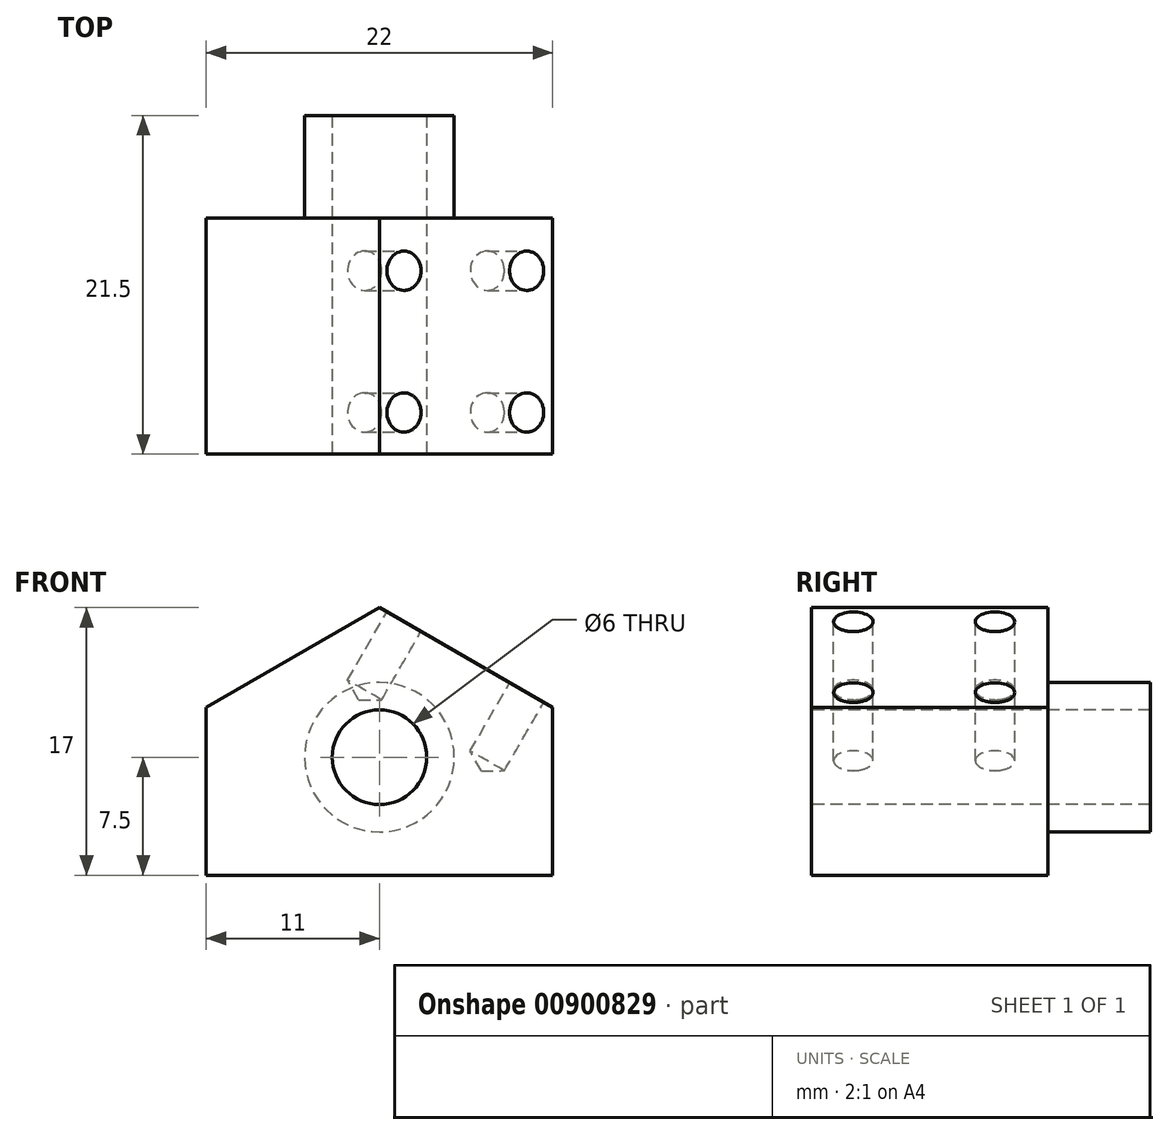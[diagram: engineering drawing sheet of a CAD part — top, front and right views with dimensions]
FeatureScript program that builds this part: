
annotation { "Feature Type Name" : "Feature", "Feature Type Description" : "" }
export const myFeature = defineFeature(function(context is Context, id is Id, definition is map)
    precondition{}
    {
        {
            var Q0;
            Q0=qCreatedBy(makeId("Front.planeOp"),FACE);
            var sketch = newSketch(context, id + "F0", { "sketchPlane" : qUnion([Q0])});
            skLineSegment(sketch, "E0.bottom", {"start": v(-11, 0) * mm, "end": v(11, 0) * mm});
            skLineSegment(sketch, "E0.top", {"start": v(-11, 17) * mm, "end": v(11, 17) * mm});
            skLineSegment(sketch, "E0.left", {"start": v(-11, 0) * mm, "end": v(-11, 17) * mm});
            skLineSegment(sketch, "E0.right", {"start": v(11, 0) * mm, "end": v(11, 17) * mm});
            skPoint(sketch, "E1", {"position": v(0, 0) * mm});
            skSolve(sketch);
        }
        {
            var Q0;
            Q0=makeQuery(id+"F0.imprint","IMPRINT",FACE,{"disambiguationData":[TD([[makeQuery(id+"F0.imprint","IMPRINT",EDGE,{"derivedFrom":sQuery(id+"F0.wireOp",EDGE,"E0.bottom")}),1.0]])]});
            extrude(context, id + "F1", {"entities" : qUnion([Q0]), "oppositeDirection" : true, "depth" : 15 * mm, "offsetDistance" : 25 * mm});
        }
        {
            var Q0;
            Q0=makeQuery(id+"F1.opExtrude","CAP_FACE",FACE,{"disambiguationData":[OSD([sQuery(id+"F0.wireOp",EDGE,"E0.bottom"),sQuery(id+"F0.wireOp",EDGE,"E0.top"),sQuery(id+"F0.wireOp",EDGE,"E0.left"),sQuery(id+"F0.wireOp",EDGE,"E0.right")])],"isStart":false});
            var sketch = newSketch(context, id + "F2", { "sketchPlane" : qUnion([Q0])});
            skCircle(sketch, "E2", {"center": v(0, 7.5) * mm, "radius": 4.75 * mm});
            skPoint(sketch, "E2.centerSnap0", {"position": v(0, 0) * mm});
            skSolve(sketch);
        }
        {
            var Q0;
            Q0 = qSketchRegion(id + "F2", true);
            extrude(context, id + "F3", {"entities" : qUnion([Q0]), "operationType" : NewBodyOperationType.ADD, "depth" : 6.5 * mm, "offsetDistance" : 25 * mm});
        }
        {
            var Q0;
            Q0=makeQuery(id+"F0.imprint","IMPRINT",FACE,{"disambiguationData":[TD([[makeQuery(id+"F0.imprint","IMPRINT",EDGE,{"derivedFrom":sQuery(id+"F0.wireOp",EDGE,"E0.bottom")}),1.0]])]});
            var sketch = newSketch(context, id + "F4", { "sketchPlane" : qUnion([Q0])});
            skCircle(sketch, "E3", {"center": v(0, 7.5) * mm, "radius": 3 * mm});
            skSolve(sketch);
        }
        {
            var Q0;
            Q0 = qSketchRegion(id + "F4", true);
            var Q1;
            Q1=makeQuery(id+"F3.opExtrude","CAP_FACE",FACE,{"disambiguationData":[OSD([sQuery(id+"F2.wireOp",EDGE,"E2")])],"isStart":false});
            extrude(context, id + "F5", {"entities" : qUnion([Q0]), "operationType" : NewBodyOperationType.REMOVE, "endBound" : BoundingType.THROUGH_ALL, "oppositeDirection" : true, "depth" : 25 * mm, "endBoundEntityFace" : qUnion([Q1]), "offsetDistance" : 25 * mm});
        }
        {
            var Q0;
            Q0=makeQuery(id+"F0.imprint","IMPRINT",FACE,{"disambiguationData":[TD([[makeQuery(id+"F0.imprint","IMPRINT",EDGE,{"derivedFrom":sQuery(id+"F0.wireOp",EDGE,"E0.bottom")}),1.0]])]});
            var sketch = newSketch(context, id + "F6", { "sketchPlane" : qUnion([Q0])});
            skPoint(sketch, "E4", {"position": v(0, 17) * mm});
            skLineSegment(sketch, "E5", {"start": v(0, 17) * mm, "end": v(11, 10.65) * mm});
            skLineSegment(sketch, "E6", {"start": v(0, 17) * mm, "end": v(-11, 10.65) * mm});
            skLineSegment(sketch, "E7", {"start": v(0, 17) * mm, "end": v(0, 0) * mm, "construction": true});
            skLineSegment(sketch, "E8", {"start": v(-11, 10.65) * mm, "end": v(-11, 17) * mm});
            skLineSegment(sketch, "E9", {"start": v(-11, 17) * mm, "end": v(11, 17) * mm});
            skLineSegment(sketch, "E10", {"start": v(11, 17) * mm, "end": v(11, 10.65) * mm});
            skSolve(sketch);
        }
        {
            var Q0;
            Q0 = qSketchRegion(id + "F6", true);
            extrude(context, id + "F7", {"entities" : qUnion([Q0]), "operationType" : NewBodyOperationType.REMOVE, "endBound" : BoundingType.THROUGH_ALL, "oppositeDirection" : true, "depth" : 25 * mm, "offsetDistance" : 25 * mm});
        }
        {
            var Q0;
            Q0=makeQuery(id+"F7.boolean.opBoolean","COPY",FACE,{"derivedFrom":makeQuery(id+"F7.opExtrude","SWEPT_FACE",FACE,{"disambiguationData":[OSD([sQuery(id+"F6.wireOp",EDGE,"E5")])]})});
            var sketch = newSketch(context, id + "F8", { "sketchPlane" : qUnion([Q0])});
            skLineSegment(sketch, "E11.bottom", {"start": v(-6.7, 2.65) * mm, "end": v(2.3, 2.65) * mm, "construction": true});
            skLineSegment(sketch, "E11.top", {"start": v(-6.7, 11.65) * mm, "end": v(2.3, 11.65) * mm, "construction": true});
            skLineSegment(sketch, "E11.left", {"start": v(-6.7, 2.65) * mm, "end": v(-6.7, 11.65) * mm, "construction": true});
            skLineSegment(sketch, "E11.right", {"start": v(2.3, 2.65) * mm, "end": v(2.3, 11.65) * mm, "construction": true});
            skPoint(sketch, "E12", {"position": v(-6.7, 2.65) * mm});
            skPoint(sketch, "E13", {"position": v(-6.7, 11.65) * mm});
            skPoint(sketch, "E14", {"position": v(2.3, 11.65) * mm});
            skPoint(sketch, "E15", {"position": v(2.3, 2.65) * mm});
            skSolve(sketch);
        }
        {
            var Q0;
            Q0=sQuery(id+"F8.wireOp",VERTEX,"E12");
            var Q1;
            Q1=sQuery(id+"F8.wireOp",VERTEX,"E13");
            var Q2;
            Q2=sQuery(id+"F8.wireOp",VERTEX,"E14");
            var Q3;
            Q3=sQuery(id+"F8.wireOp",VERTEX,"E15");
            var Q4;
            Q4=makeQuery(id+"F1.opExtrude","SWEPT_BODY",BODY,{"disambiguationData":[OSD([sQuery(id+"F0.wireOp",EDGE,"E0.bottom"),sQuery(id+"F0.wireOp",EDGE,"E0.top"),sQuery(id+"F0.wireOp",EDGE,"E0.left"),sQuery(id+"F0.wireOp",EDGE,"E0.right")])]});
            hole(context, id + "F9", {"style" : HoleStyle.SIMPLE, "endStyle" : HoleEndStyle.BLIND, "standardTappedOrClearance" : lookupTablePath({ "standard" : "ISO", "engagement" : "75%", "pitch" : "0.5 mm", "size" : "M3", "type" : "Tapped" }), "standardBlindInLast" : lookupTablePath({ "standard" : "ISO", "engagement" : "75%", "pitch" : "0.5 mm", "size" : "M3", "type" : "Tapped" }), "holeDiameter" : 2.5 * mm, "majorDiameter" : 3 * mm, "showTappedDepth" : true, "holeDepth" : 5 * mm, "isTappedThrough" : true, "tappedDepth" : 3.5 * mm, "tapClearance" : 3, "locations" : qUnion([Q0, Q1, Q2, Q3]), "scope" : qUnion([Q4])});
        }
    });
